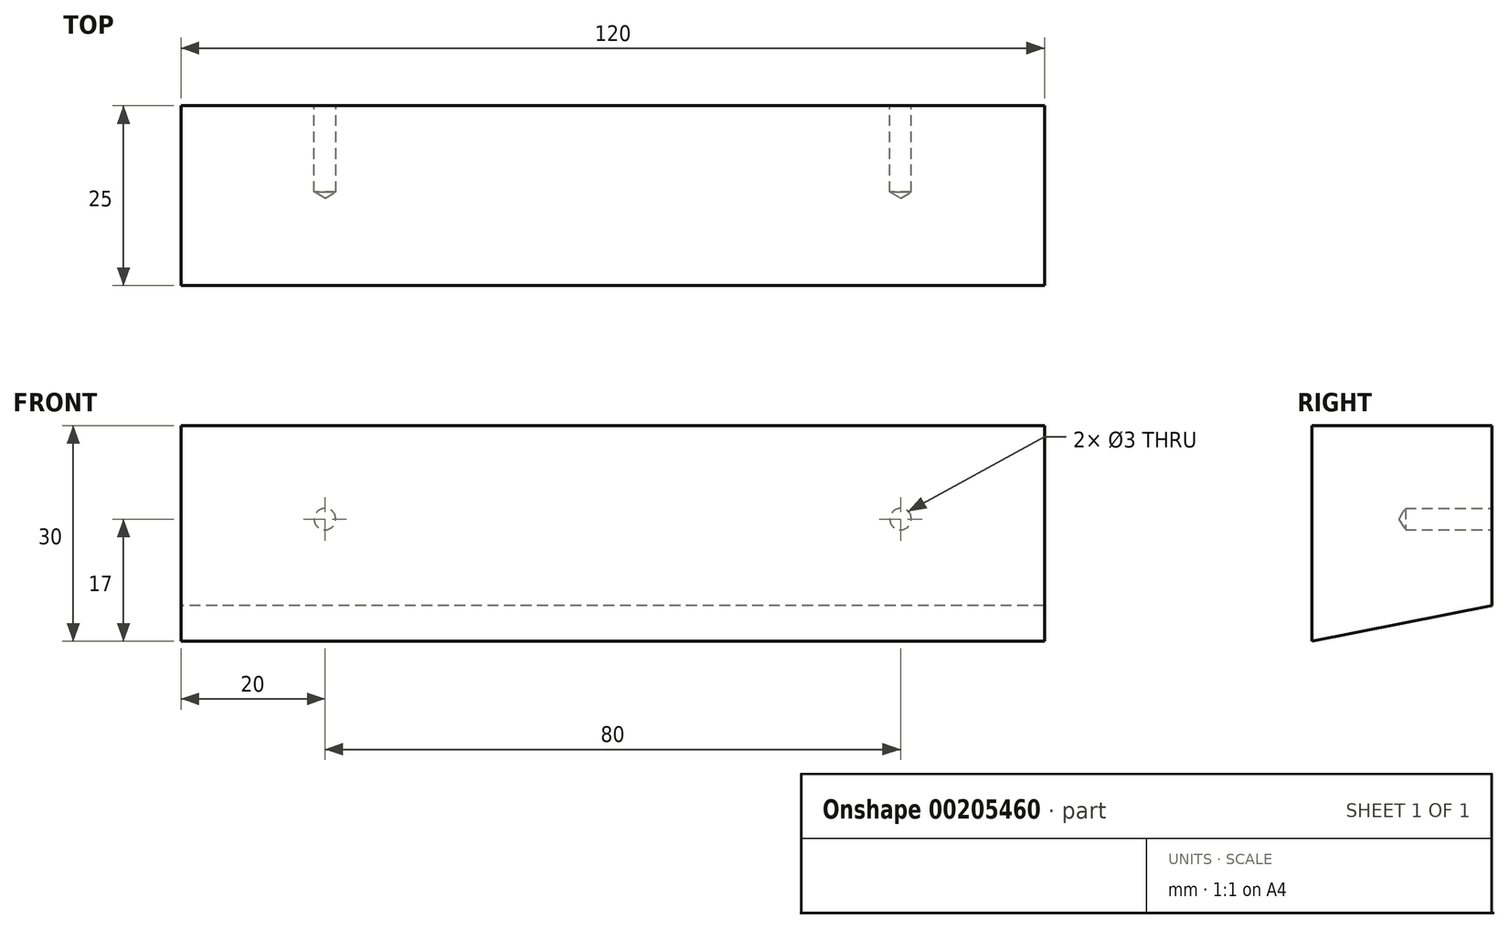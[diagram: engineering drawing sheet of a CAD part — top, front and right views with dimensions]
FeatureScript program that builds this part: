
annotation { "Feature Type Name" : "Feature", "Feature Type Description" : "" }
export const myFeature = defineFeature(function(context is Context, id is Id, definition is map)
    precondition{}
    {
        {
            var Q0;
            Q0=qCreatedBy(makeId("Right.planeOp"),FACE);
            var sketch = newSketch(context, id + "F0", { "sketchPlane" : qUnion([Q0])});
            skLineSegment(sketch, "E0", {"start": v(0, 0) * mm, "end": v(0, 30) * mm});
            skLineSegment(sketch, "E1", {"start": v(0, 30) * mm, "end": v(25, 30) * mm});
            skLineSegment(sketch, "E2", {"start": v(0, 0) * mm, "end": v(25, 5) * mm});
            skLineSegment(sketch, "E3", {"start": v(25, 5) * mm, "end": v(25, 30) * mm});
            skSolve(sketch);
        }
        {
            var Q0;
            Q0=makeQuery(id+"F0.imprint","IMPRINT",FACE,{"disambiguationData":[TD([[makeQuery(id+"F0.imprint","IMPRINT",EDGE,{"derivedFrom":sQuery(id+"F0.wireOp",EDGE,"E0")}),-1.0]])]});
            extrude(context, id + "F1", {"entities" : qUnion([Q0]), "depth" : 120 * mm, "symmetric" : true});
        }
        {
            var Q0;
            Q0=makeQuery(id+"F1.opExtrude","SWEPT_FACE",FACE,{"disambiguationData":[OSD([sQuery(id+"F0.wireOp",EDGE,"E3")])]});
            var sketch = newSketch(context, id + "F2", { "sketchPlane" : qUnion([Q0])});
            skPoint(sketch, "E4", {"position": v(-40, 17) * mm});
            skPoint(sketch, "E5", {"position": v(40, 17) * mm});
            skLineSegment(sketch, "E6", {"start": v(-40, 17) * mm, "end": v(40, 17) * mm, "construction": true});
            skSolve(sketch);
        }
        {
            var Q0;
            Q0=sQuery(id+"F2.wireOp",VERTEX,"E4");
            var Q1;
            Q1=sQuery(id+"F2.wireOp",VERTEX,"E5");
            var Q2;
            Q2=makeQuery(id+"F1.opExtrude","SWEPT_BODY",BODY,{"disambiguationData":[OSD([sQuery(id+"F0.wireOp",EDGE,"E0"),sQuery(id+"F0.wireOp",EDGE,"E1"),sQuery(id+"F0.wireOp",EDGE,"E2"),sQuery(id+"F0.wireOp",EDGE,"E3")])]});
            hole(context, id + "F3", {"style" : HoleStyle.SIMPLE, "endStyle" : HoleEndStyle.BLIND, "standardTappedOrClearance" : lookupTablePath({ "standard" : "ISO", "size" : "3", "type" : "Drilled" }), "standardBlindInLast" : lookupTablePath({ "standard" : "ISO", "size" : "3", "type" : "Drilled" }), "holeDiameter" : 3 * mm, "holeDepth" : 12 * mm, "locations" : qUnion([Q0, Q1]), "scope" : qUnion([Q2])});
        }
    });
